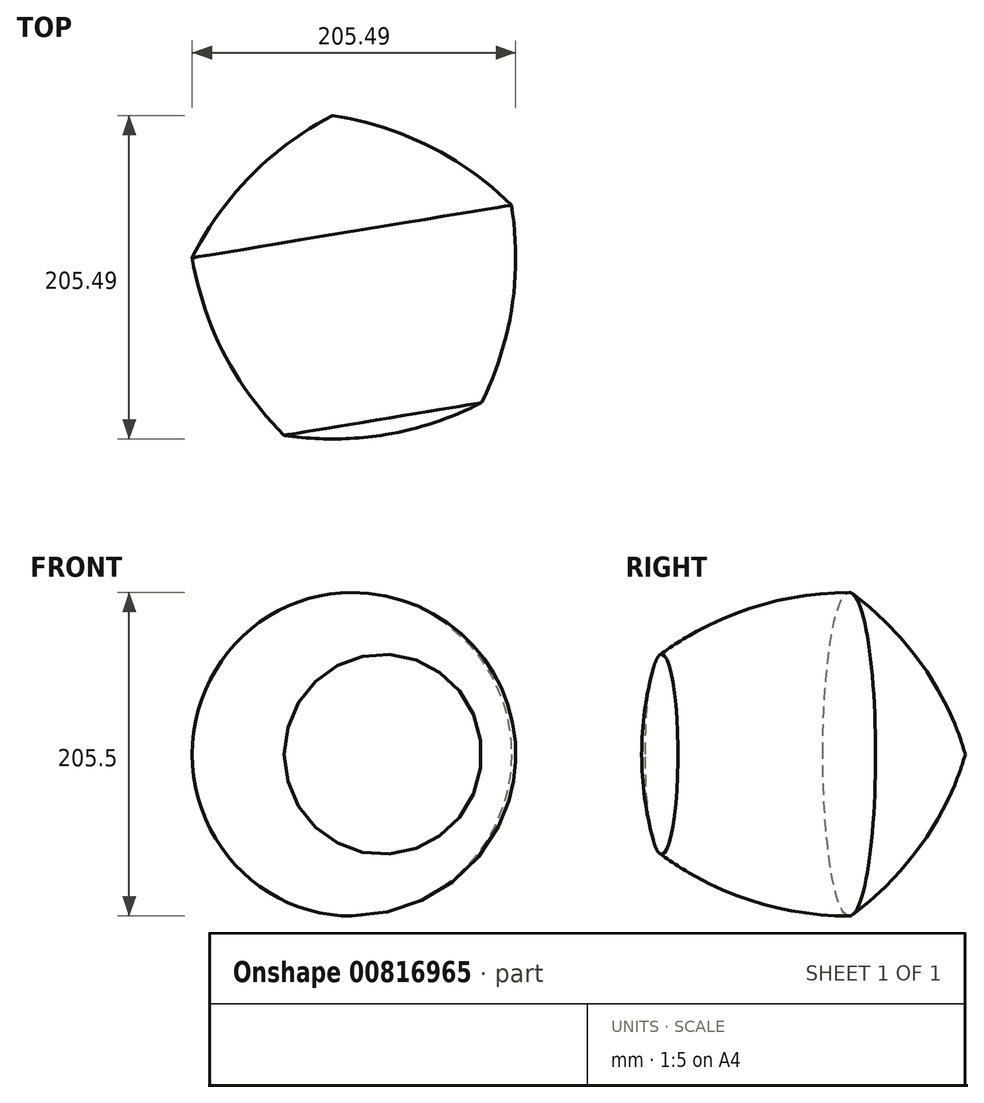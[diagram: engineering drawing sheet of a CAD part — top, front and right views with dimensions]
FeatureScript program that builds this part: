
annotation { "Feature Type Name" : "Feature", "Feature Type Description" : "" }
export const myFeature = defineFeature(function(context is Context, id is Id, definition is map)
    precondition{}
    {
        {
            var Q0;
            Q0=qCreatedBy(makeId("Top.planeOp"),FACE);
            var sketch = newSketch(context, id + "F0", { "sketchPlane" : qUnion([Q0])});
            skPoint(sketch, "E0.0.midPoint", {"position": v(-62.2, 61.4) * mm});
            skArc(sketch, "E1", {"start": v(-106.81, 16.2) * mm, "mid": v(-86.54, -44.82) * mm, "end": v(-48.41, -96.58) * mm});
            skPoint(sketch, "E2", {"position": v(-48.41, -96.58) * mm});
            skPoint(sketch, "E3", {"position": v(14.24, -86.23) * mm});
            skLineSegment(sketch, "E4", {"start": v(14.24, -86.23) * mm, "end": v(-17.6, 106.59) * mm});
            skLineSegment(sketch, "E5", {"start": v(-17.6, 106.59) * mm, "end": v(15.88, -96.16) * mm});
            skArc(sketch, "E6.trimOffspring", {"start": v(-48.41, -96.58) * mm, "mid": v(-16.25, -98.9) * mm, "end": v(15.88, -96.16) * mm});
            skArc(sketch, "E7.trimOffspring", {"start": v(-17.6, 106.59) * mm, "mid": v(-69.36, 68.46) * mm, "end": v(-106.81, 16.2) * mm});
            skSolve(sketch);
        }
        {
            var Q0;
            Q0 = qSketchRegion(id + "F0", true);
            var Q1;
            Q1=sQuery(id+"F0.wireOp",EDGE,"E5");
            revolve(context, id + "F1", {"surfaceOperationType" : NewSurfaceOperationType.NEW, "entities" : qUnion([Q0]), "axis" : qUnion([Q1]), "revolveType" : RevolveType.FULL});
        }
    });
